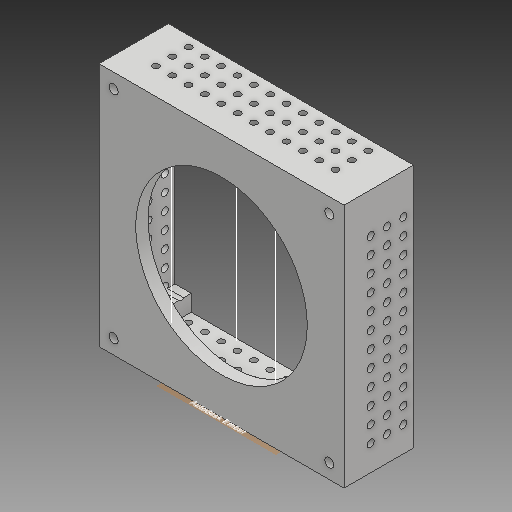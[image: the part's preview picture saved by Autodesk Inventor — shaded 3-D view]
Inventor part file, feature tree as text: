
AUTODESK INVENTOR PART (.ipt)
format: ipt  version: 2018 (Build 220112000, 112)  size: 655,872 bytes
history: native  units: mm
features: sketch x9, extrude x7, pattern_linear x4
ambient origin geometry x8: Origin, YZ Plane, XZ Plane, XY Plane, X Axis, Y Axis, Z Axis, Center Point
bodies: Solid1 (feature_tree)
feature tree (20):
  sketch  "Sketch1"  dims[d0=150.0mm d1=150.0mm]
  extrude  "Extrusion1"  Depth=150.0mm
  extrude  "Extrusion2"  Depth=7.5mm TaperAngle=0.0deg
  extrude  "Extrusion3"  Depth=35.0mm TaperAngle=0.0deg
  extrude  "Extrusion4"  Depth=10.0mm
  pattern_linear  "Rectangular Pattern1"  Count1=2 Spacing1=132.0mm
  extrude  "Extrusion5"  Depth=132.0mm
  pattern_linear  "Rectangular Pattern2"  Count1=8 Spacing1=0.0mm
  extrude  "Extrusion6"  Depth=132.0mm
  pattern_linear  "Rectangular Pattern3"  Count1=30 Spacing1=0.0mm
  extrude  "Extrusion7"  Depth=10.0mm
  pattern_linear  "Rectangular Pattern4"  Count1=30 Spacing1=0.0mm
  sketch  "Sketch9"  dims[d39=120.0mm d41=10.0mm d42=30.0mm d44=10.0mm]
  sketch  "Sketch2"  dims[d2=7.5mm d3=0.0mm d5=7.5mm d6=0.0mm]
  sketch  "Sketch3"  dims[d7=4.0mm d8=35.0mm d9=0.0mm]
  sketch  "Sketch4"  dims[d10=10.0mm d11=10.0mm]
  sketch  "Sketch5"  dims[d12=35.0mm d13=0.0mm d14=20.0mm d16=132.0mm]
  sketch  "Sketch6"  dims[d17=20.0mm d19=132.0mm d20=5.5mm d21=80.0mm d22=0.0mm]
  sketch  "Sketch7"  dims[d23=20.0mm d25=132.0mm d26=20.0mm d28=132.0mm d29=300.0mm d30=0.0mm]
  sketch  "Sketch8"  dims[d31=120.0mm d33=10.0mm d34=30.0mm d36=10.0mm d37=300.0mm d38=0.0mm]
